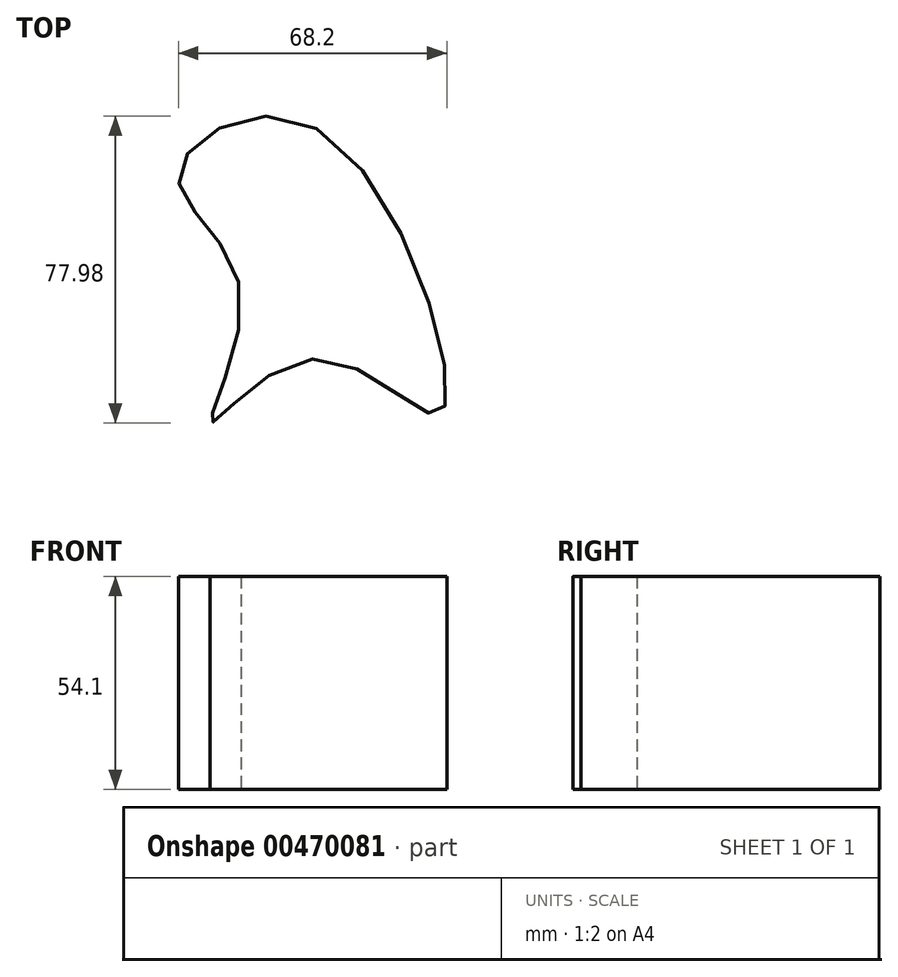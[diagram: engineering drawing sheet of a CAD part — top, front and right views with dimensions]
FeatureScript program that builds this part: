
annotation { "Feature Type Name" : "Feature", "Feature Type Description" : "" }
export const myFeature = defineFeature(function(context is Context, id is Id, definition is map)
    precondition{}
    {
        {
            var Q0;
            Q0=qCreatedBy(makeId("Top.planeOp"),FACE);
            var sketch = newSketch(context, id + "F0", { "sketchPlane" : qUnion([Q0])});
            skFitSpline(sketch, "E0", {"points": [v(0, 40.57) * mm, v(-35.01, 29.09) * mm, v(-19.45, 0) * mm, v(-26.86, -34.27) * mm, v(0, -17.97) * mm, v(31.68, -31.68) * mm, v(0, 40.57) * mm]});
            skSolve(sketch);
        }
        {
            var Q0;
            Q0=makeQuery(id+"F0.imprint","IMPRINT",FACE,{"disambiguationData":[TD([[makeQuery(id+"F0.imprint","IMPRINT",EDGE,{"derivedFrom":sQuery(id+"F0.wireOp",EDGE,"E0")}),1.0]])]});
            extrude(context, id + "F1", {"entities" : qUnion([Q0]), "depth" : 54.1 * mm});
        }
    });
